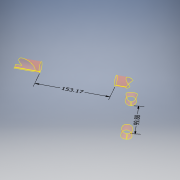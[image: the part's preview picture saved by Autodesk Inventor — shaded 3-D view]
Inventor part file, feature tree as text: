
AUTODESK INVENTOR PART (.ipt)
format: ipt  version: 2018 (Build 220112000, 112)  size: 327,168 bytes
history: native  units: mm
features: other x13, sketch x6, extrude x4, surface_op x4, plane x3, delete_face x3, boolean_combine x2, direct_edit x2, move_body x2
ambient origin geometry x8: Origin, YZ Plane, XZ Plane, XY Plane, X Axis, Y Axis, Z Axis, Center Point
bodies: Solid3 (feature_tree), Solid2 (feature_tree), Solid4 (feature_tree)
feature tree (39):
  other  "Swingarm.ipt"
  other  "Swingarm2.ipt"
  other  "Annotations"
  extrude  "Extrusion1"  Depth=10.0mm TaperAngle=0.0deg
  plane  "Work Plane2"
  extrude  "Extrusion2"  TaperAngle=0.0deg  [1 undecoded]
  plane  "Work Plane4"
  extrude  "Extrusion5"  TaperAngle=0.0deg  [1 undecoded]
  boolean_combine  "Combine3"
  direct_edit  "Direct Edit1"
  extrude  "Extrusion6"  Depth=1.0mm
  direct_edit  "Direct Edit2"
  boolean_combine  "Combine2"
  delete_face  "Delete Face2"
  delete_face  "Delete Face4"
  delete_face  "Delete Face5"
  sketch  "Sketch3"  dims[d9=0.0mm d10=0.0mm]
  surface_op  "Trim1"
  surface_op  "Trim2"
  sketch  "Sketch8"  dims[d21=10.0mm d22=187.0mm d25=61.5mm d26=0.0mm d27=0.0mm d28=0.0mm d29=0.0mm d30=0.0mm d31=0.0mm d32=0.0mm d33=-31.5mm d34=35.75mm d35=0.0mm d36=0.0mm d37=0.0mm d38=7.75mm d39=1.0mm d40=1.0mm d41=153.165097mm d42=99.875mm]
  surface_op  "Trim3"
  surface_op  "Trim4"
  other  "Arms::Swingarm.ipt"
  other  "TaggingFeature2"
  sketch  "Sketch1"  dims[d1=10.0mm d2=52.5mm d3=0.0mm]
  sketch  "Sketch2"  dims[d6=64.5mm d7=0.0mm d8=0.0mm]
  other  "Solid6::Swingarm2.ipt"
  other  "TaggingFeature3"
  plane  "Work Plane2_1"
  sketch  "Sketch5"  dims[d11=0.0mm d12=1.0mm]
  sketch  "Sketch7"  dims[d13=3.0mm]
  other  "OffsetSrf2"
  other  "OffsetSrf3"
  other  "OffsetSrf4"
  other  "OffsetSrf5"
  move_body  "Move1"
  move_body  "Move2"
  other  "Linear Dimension 1"
  other  "Linear Dimension 2"
note: 2 required parameter values undecoded (feature->parameter linkage not recoverable at this tier; creation-order binding heuristic only, values carry confidence <= 0.55)
